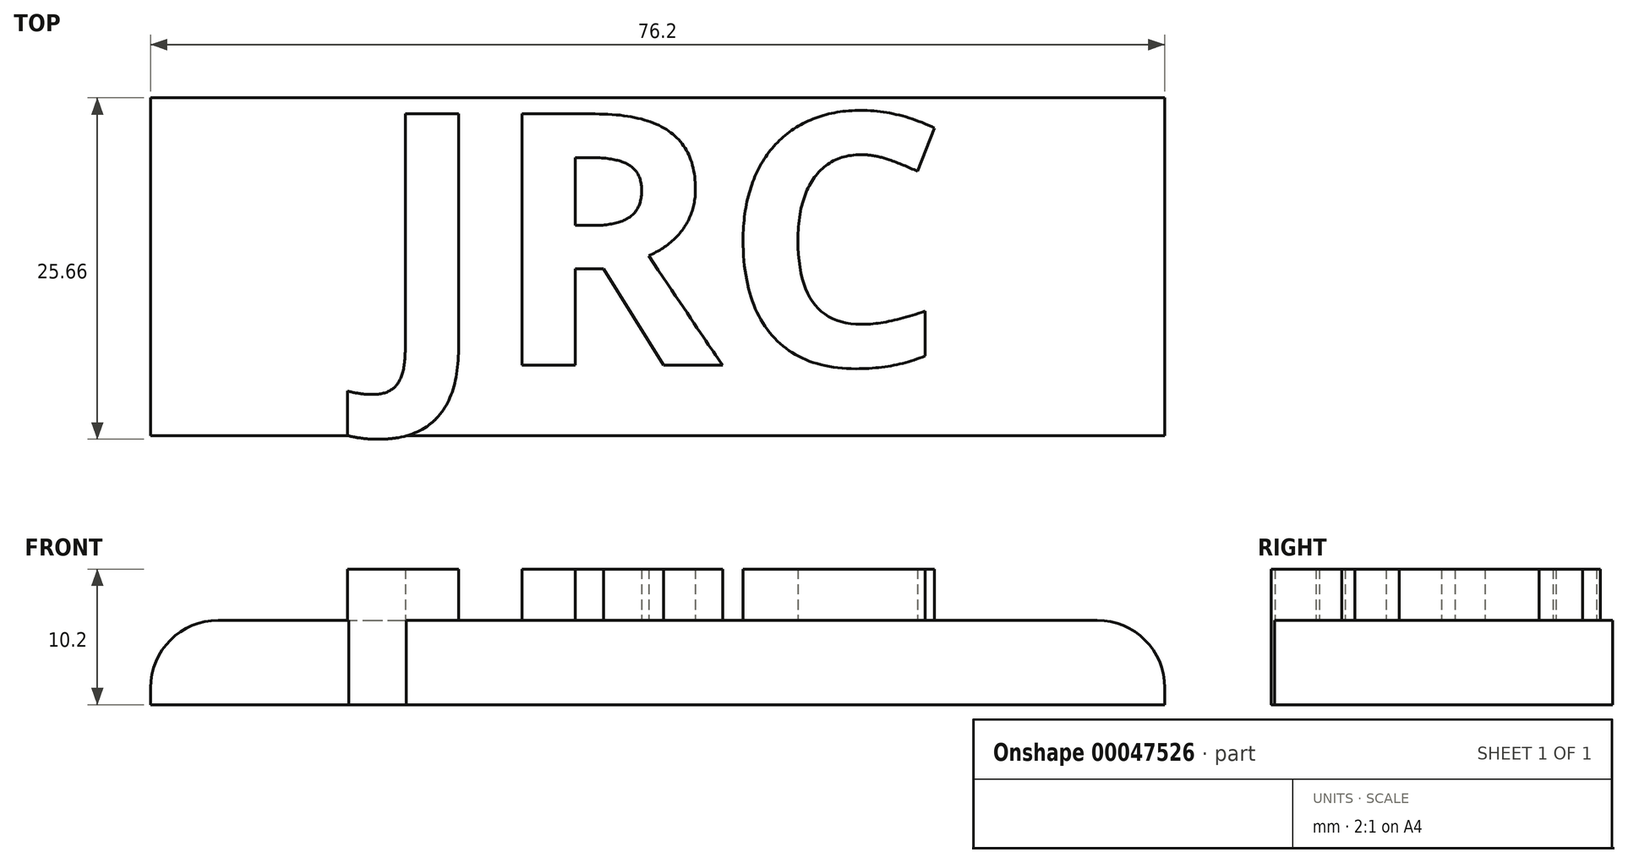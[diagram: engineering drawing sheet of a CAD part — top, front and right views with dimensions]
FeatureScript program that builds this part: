
annotation { "Feature Type Name" : "Feature", "Feature Type Description" : "" }
export const myFeature = defineFeature(function(context is Context, id is Id, definition is map)
    precondition{}
    {
        {
            var Q0;
            Q0=qCreatedBy(makeId("Top.planeOp"),FACE);
            var sketch = newSketch(context, id + "F0", { "sketchPlane" : qUnion([Q0])});
            skLineSegment(sketch, "E0.rect.bottom", {"start": v(38.1, -12.7) * mm, "end": v(-38.1, -12.7) * mm});
            skLineSegment(sketch, "E0.rect.top", {"start": v(38.1, 12.7) * mm, "end": v(-38.1, 12.7) * mm});
            skLineSegment(sketch, "E0.rect.left", {"start": v(38.1, -12.7) * mm, "end": v(38.1, 12.7) * mm});
            skLineSegment(sketch, "E0.rect.right", {"start": v(-38.1, -12.7) * mm, "end": v(-38.1, 12.7) * mm});
            skPoint(sketch, "E0.rect.middle", {"position": v(0, 0) * mm});
            skSolve(sketch);
        }
        {
            var Q0;
            Q0=makeQuery(id+"F0.imprint","IMPRINT",FACE,{"disambiguationData":[TD([[makeQuery(id+"F0.imprint","IMPRINT",EDGE,{"derivedFrom":sQuery(id+"F0.wireOp",EDGE,"E0.rect.bottom")}),-1.0]])]});
            extrude(context, id + "F1", {"entities" : qUnion([Q0]), "depth" : 6.35 * mm});
        }
        {
            var Q0;
            Q0=qCreatedBy(makeId("Top.planeOp"),FACE);
            var sketch = newSketch(context, id + "F2", { "sketchPlane" : qUnion([Q0])});
            skText(sketch, "E1", { "text": "JRC", "fontName": "OpenSans-Bold.ttf"});
            const initialGuessF2  = {"E1": [-0.02135, -0.0074, 1, 0, 0.01905]};
            skSetInitialGuess(sketch, initialGuessF2);
            skSolve(sketch);
        }
        {
            var Q0;
            Q0 = qSketchRegion(id + "F2", true);
            extrude(context, id + "F3", {"entities" : qUnion([Q0]), "operationType" : NewBodyOperationType.ADD, "depth" : 10.2 * mm});
        }
        {
            var Q0;
            Q0=makeQuery(id+"F1.opExtrude","CAP_EDGE",EDGE,{"disambiguationData":[OSD([sQuery(id+"F0.wireOp",EDGE,"E0.rect.right")])],"isStart":false});
            var Q1;
            Q1=makeQuery(id+"F1.opExtrude","CAP_EDGE",EDGE,{"disambiguationData":[OSD([sQuery(id+"F0.wireOp",EDGE,"E0.rect.left")])],"isStart":false});
            fillet(context, id + "F4", {"entities" : qUnion([Q0, Q1]), "radius" : 5.08 * mm, "tangentPropagation" : true, "allowEdgeOverflow" : false});
        }
    });
